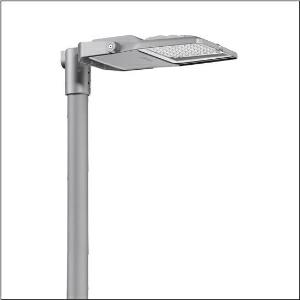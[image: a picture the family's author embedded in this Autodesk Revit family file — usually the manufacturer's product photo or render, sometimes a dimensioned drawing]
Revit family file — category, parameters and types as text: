
# Revit family: floodlight_fl_21_iq_mini___pl61_5xa7772d2c3a_9c70
name_source: partatom
category: Lighting Fixtures
units: mm (PartAtom-declared; Revit-internal decimal feet)

## family parameters
Cut with Voids When Loaded = No
Host = Face
Light Source = No
Part Type = Normal
Room Calculation Point = No
Round Connector Dimension = Use Diameter
Shared = No

## types (1)
- --- (1 x LED, 17500 lm, 143 W, 3000K)
    Apparent Load = 143 VA
    CIE Flux Codes = 33 65 98 100 100
    Color Rendering = 70
    Color Temperature = 3000K
    Default Elevation = 1800 mm
    Description = Floodlight FL 21 iQ mini, floodlight, primary light control with lens, of PMMA, primary optical cover: protective disc, of toughened safety glass, transparent, light distribution: PL61, light emission: direct distribution, installation type: surface-mounted, LED, High Power LED, rated luminous flux: 17.500lm, luminous efficacy: 122lm/W, light colour: 730, colour temperature: 3000K, control: Auto-Match, Temp-Guard, Night-Set, Smart-Wire, Desk-Remote (wireless, voltage-free reading and setting of iQ features in the workshop via application-optimized NFC function/RFID function), optimised constant luminous flux control (CLO 2.0), Light-Fading, Lumen-Switch, with terminal, 6-pole, mains connection: 220..240V, AC, 50/60Hz, start of lifetime: 143W, end of service life: 152W, reduction: 61W, luminaire housing, of diecast aluminium, powder-coated, Siteco® metallic grey (DB 702S), corrosivity category C5 mid according to DIN EN ISO 12944, sealing non-destructively replaceable, please order mast flange separately, mast bracket, of steel, galvanised, powder-coated, protection rating (complete): IP66, insulation class (complete): insulation class II (safety insulation), certification: CE, ENEC, VDE, protection symbol: D, impact resistance: IK08, permissible operating ambient temperature: -40..+40°C, permissible operating ambient temperature for outdoor applications: -40..+50°C, standard: DIN EN 12944, LABS conformity tested according to VDMA 24364:2018-05, packaging unit: 1 piece

Light Distribution: PL61
    Height = 70 mm
    Lamp = 1 x LED
    Lamp Light Flux = 17500 lm
    Lamp Power = 143 W
    Lamp count = 1
    Length = 485 mm
    Luminous efficacy = 122 lm/W
    Manufacturer = Siteco
    ModVariant = No
    Model = 5XA7772D2C3A
    Number of Poles = 1
    OnlyDefault = Yes
    Power Factor = 1
    Product Name = Floodlight FL 21 iQ mini | PL61
    Product group = floodlight | pylon annexe
    ProductGroupID = 6200
    Protection Class = Protection class II
    Protection Degree = IP 66
    RLX_Detail_Level = 1
    RLX_Emergency_Light_Flux = 0 lm
    RLX_Emergency_Type = 0
    RLX_Emergency_Type_DB = No
    RlxData = <blob elided: 101597 chars, md5=cbf14f53>
    Socket = socket
    Standby Power = 0 W
    System Light Flux = 17500 lm
    System Power = 143 W
    Type Comments = factory setting: luminous flux: 100 % | dim-lin: 254 | 730 mA
    Type Image = l_1007125.jpg
    URL = http://relux.com
    VarID = @adj_143561
    Voltage = 0 V
    Weight = 0.00 kg
    Width = 337 mm

## geometry (parser evidence)
native form markers: Blend x4, Sweep x13
no freeform markers — native parametric forms only
